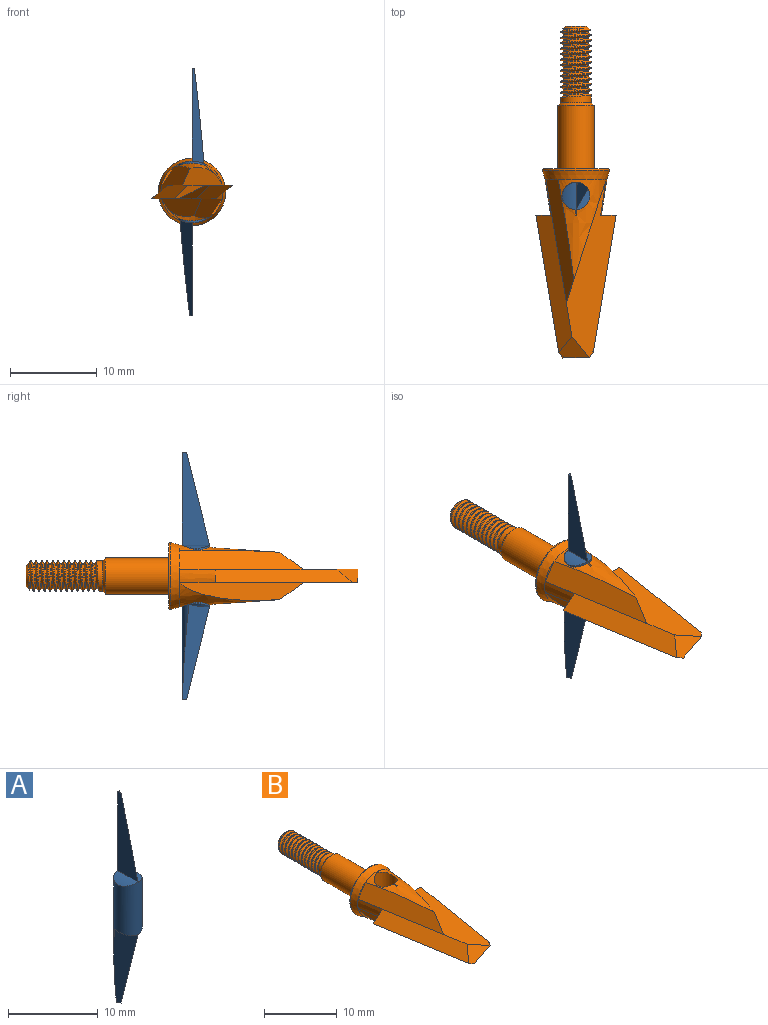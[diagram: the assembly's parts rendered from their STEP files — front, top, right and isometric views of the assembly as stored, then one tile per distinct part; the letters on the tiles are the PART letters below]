
ASSEMBLY  parts=2 mates=1
PART A: 13 faces, bbox 3.3x3.3x28.7 mm
  f0: cylinder r=1.59mm len=28.58mm, axis (0,0,-1), area 87.8mm2, adj f1,f2,f3,f4,f6,f7,f8,f9
  f1: cylinder r=3.56mm len=2.38mm, axis (0,1,0), area 1.6mm2, adj f0,f5,f9,f12
  f2: plane 10.73x3.18mm, normal (-1,0,0), area 19.8mm2, adj f0,f4,f7,f11
  f3: cylinder r=3.56mm len=3.18mm, axis (0,1,0), area 4.1mm2, adj f0,f6
  f4: plane 11.09x3.24mm, normal (0.87,-0.49,0.12), area 19.3mm2, adj f0,f2,f8,f11
  f5: plane 0.07x0.04mm, normal (-0.5,0.86,0.12), area 0mm2, adj f1,f9,f12
  f6: plane 10.73x3.18mm, normal (1,0,0), area 19.8mm2, adj f0,f3,f9,f10
  f7: cylinder r=3.56mm len=3.18mm, axis (0,1,0), area 4.1mm2, adj f0,f2
  f8: cylinder r=3.56mm len=2.38mm, axis (0,1,0), area 1.6mm2, adj f0,f4
  f9: plane 11.03x3.17mm, normal (-0.87,-0.49,-0.12), area 19.3mm2, adj f0,f1,f5,f6,f10,f12
  f10: plane 0.51x0.27mm, normal (0,0,-1), area 0.1mm2, adj f0,f6,f9
  f11: plane 0.51x0.27mm, normal (0,0,1), area 0.1mm2, adj f0,f2,f4
  f12: plane 1.08x0.59mm, normal (0.08,0.11,-0.99), area 0.1mm2, adj f1,f5,f9
PART B: 53 faces, bbox 9.3x275.7x8.4 mm
  f0: cylinder r=2.08mm len=7.37mm, axis (0,-1,0), area 96.4mm2, adj f2,f38
  f1: plane 3.66x3.66mm, normal (0,1,0), area 0.9mm2, adj f2,f3
  f2: cone r=1.83mm half-angle=45deg, axis (0,-1,0), area 4.4mm2, adj f0,f1
  f3: cylinder r=1.75mm len=3.51mm, axis (0,-1,0), area 7.4mm2, adj f1,f4,f18,f19,f21
  f4: cylinder r=1.75mm len=3.51mm, axis (0,-1,0), area 1mm2, adj f3,f5,f19,f21
  f5: cylinder r=1.75mm len=3.51mm, axis (0,-1,0), area 1mm2, adj f4,f6,f19,f21
  f6: cylinder r=1.75mm len=3.51mm, axis (0,-1,0), area 1mm2, adj f5,f7,f19,f21
  f7: cylinder r=1.75mm len=3.51mm, axis (0,-1,0), area 1mm2, adj f6,f8,f19,f21
  f8: cylinder r=1.75mm len=3.51mm, axis (0,-1,0), area 1mm2, adj f7,f9,f19,f21
  f9: cylinder r=1.75mm len=3.51mm, axis (0,-1,0), area 1mm2, adj f8,f10,f19,f21
  f10: cylinder r=1.75mm len=3.51mm, axis (0,-1,0), area 1mm2, adj f9,f11,f19,f21
  f11: cylinder r=1.75mm len=3.51mm, axis (0,-1,0), area 1mm2, adj f10,f12,f19,f21
  f12: cylinder r=1.75mm len=3.51mm, axis (0,-1,0), area 1mm2, adj f11,f13,f19,f21
  f13: cylinder r=1.75mm len=3.51mm, axis (0,-1,0), area 1mm2, adj f12,f14,f19,f21
  f14: cylinder r=1.75mm len=3.51mm, axis (0,-1,0), area 1mm2, adj f13,f15,f19,f21
  f15: cylinder r=1.75mm len=1.33mm, axis (0,-1,0), area 0.1mm2, adj f14,f17,f21
  f16: plane 2.49x2.49mm, normal (0,1,0), area 4.9mm2, adj f17
  f17: cone r=1.24mm half-angle=45deg, axis (0,-1,0), area 4.6mm2, adj f15,f16,f19,f20,f21
  f18: plane 0.55x0.27mm, normal (0,0,-1), area 0.1mm2, adj f3,f19,f20,f21
  f19: bspline ~8.47x4.05mm, area 45.1mm2, adj f3,f4,f5,f6,f7,f8,f9,f10
  f20: cylinder r=1.48mm len=8.16mm, axis (0,1,0), area 20.7mm2, adj f17,f18,f19,f21
  f21: bspline ~8.23x4.05mm, area 41.3mm2, adj f3,f4,f5,f6,f7,f8,f9,f10
  f22: plane 0.17x0.15mm, normal (0,1,0), area 0mm2, adj f23,f40,f41
  f23: cone r=3.56mm half-angle=4deg, axis (0,1,0), area 26.1mm2, adj f22,f24,f25,f36,f40,f41,f42
  f24: plane 14.22x4.59mm, normal (0.95,-0.31,0), area 23.2mm2, adj f23,f25,f27
  f25: plane 14.22x3.21mm, normal (-0.83,-0.14,0.54), area 33.3mm2, adj f23,f24,f33,f36,f45
  f26: plane 1.79x1.47mm, normal (0,1,0), area 1.2mm2, adj f30,f33,f46
  f27: plane 20.59x5.77mm, normal (0,0,1), area 51.8mm2, adj f24,f28,f29,f31,f32,f33,f44
  f28: plane 1.79x1.47mm, normal (0,1,0), area 1.2mm2, adj f27,f32,f44
  f29: plane 3.53x2.45mm, normal (-0.42,-0.34,0.84), area 5.5mm2, adj f27,f30,f31,f33
  f30: plane 20.59x5.77mm, normal (0,0,-1), area 51.8mm2, adj f26,f29,f31,f32,f33,f46,f49
  f31: plane 3.53x2.45mm, normal (0.42,-0.34,-0.84), area 5.5mm2, adj f27,f29,f30,f32
  f32: plane 15.92x4.17mm, normal (0.63,-0.1,-0.77), area 36mm2, adj f27,f28,f30,f31,f34,f50
  f33: plane 15.92x4.17mm, normal (-0.63,-0.1,0.77), area 36mm2, adj f25,f26,f27,f29,f30,f35
  f34: plane 0.07x0.06mm, normal (0,-1,0), area 0mm2, adj f32,f43,f44
  f35: plane 0.07x0.06mm, normal (0,-1,0), area 0mm2, adj f33,f45,f46
  f36: plane 7.15x7.15mm, normal (0,-1,0), area 1.2mm2, adj f23,f25,f37,f43,f44,f45,f46,f48
  f37: cone r=3.94mm half-angle=16deg, axis (0,1,0), area 27mm2, adj f36,f39
  f38: plane 7.54x7.54mm, normal (0,1,0), area 31mm2, adj f0,f39
  f39: torus R=3.77mm, axis (0,1,0), area 5.7mm2, adj f37,f38
  f40: bspline ~259.18x0.34mm, area 0.1mm2, adj f22,f23,f41,f42
  f41: bspline ~259.18x0.33mm, area 0.1mm2, adj f22,f23,f40,f42
  f42: cylinder r=1.59mm len=7.08mm, axis (0,0,-1), area 64.5mm2, adj f23,f40,f41,f48,f51,f52
  f43: plane 4.08x0.69mm, normal (0,0,-1), area 0.1mm2, adj f34,f36,f44,f50
  f44: cone r=3.56mm half-angle=8.5deg, axis (0,1,0), area 6.4mm2, adj f27,f28,f34,f36,f43
  f45: plane 4.08x0.69mm, normal (0,0,1), area 0.1mm2, adj f25,f35,f36,f46
  f46: cone r=3.56mm half-angle=8.5deg, axis (0,1,0), area 6.4mm2, adj f26,f30,f35,f36,f45
  f47: plane 0.17x0.15mm, normal (0,1,0), area 0mm2, adj f48,f51,f52
  f48: cone r=3.56mm half-angle=4deg, axis (0,1,0), area 26.1mm2, adj f36,f42,f47,f49,f50,f51,f52
  f49: plane 14.22x4.59mm, normal (-0.95,-0.31,0), area 23.2mm2, adj f30,f48,f50
  f50: plane 14.22x3.21mm, normal (0.83,-0.14,-0.54), area 33.3mm2, adj f32,f36,f43,f48,f49
  f51: bspline ~259.18x0.34mm, area 0.1mm2, adj f42,f47,f48,f52
  f52: bspline ~259.18x0.33mm, area 0.1mm2, adj f42,f47,f48,f51
PLACE A t=(0,2.21,0)mm
PLACE B at identity fixed
MATE cylindrical B.f42 <-> A.f0  axis (0,0,-1) through (0,2.21,0)mm
